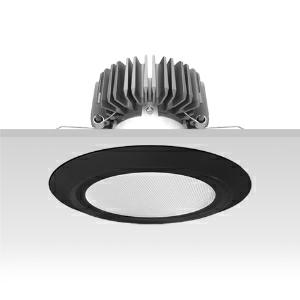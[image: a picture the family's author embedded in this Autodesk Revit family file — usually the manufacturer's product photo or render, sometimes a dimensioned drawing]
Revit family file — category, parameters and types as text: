
# Revit family: 3f_filippi_-_3f_reno_bianco_ampio_3f_filippi_-_30691_a01049_-_3f_reno_200_wh_4000-930_dali_wide___smp_bk_4fdb
name_source: partatom
category: Lighting Fixtures
units: mm (PartAtom-declared; Revit-internal decimal feet)

## family parameters
Cut with Voids When Loaded = No
Host = Face
Light Source = No
Part Type = Normal
Room Calculation Point = No
Round Connector Dimension = Use Diameter
Shared = No

## types (1)
- 3F Filippi - 3F Reno Bianco Ampio (1 x LED, 2801 lm, 43 W, 3000 K)
    Apparent Load = 43 VA
    Approval mark = CE
    CIE Flux Codes = 74 92 98 100 100
    Color Rendering = 90
    Color Temperature = 3000 K
    Control Gear = Electronic transformer
    Default Elevation = 1800 mm
    Description = ILLUMINOTECHNICAL
Luminous efficiency 100% (DLOR 100%, ULOR 0%).
Initial luminous flux of the luminaire 2801 lm.
Direct symmetric wide distribution.
Installation Interdistance Transv.D = 1.06 x hu - Long.D = 1.04 x hu.
Tabular UGR (CIE 117 - 4H-8H; S=0.25H; 70/50/20): RUG 23.1 - 23.
Beam angle: 70° - 69°.
Luminous efficacy 65 lm/W.
Lifetime (L90/B10): 30000 h. (tq+25°C)
Lifetime (L85/B10): 50000 h. (tq+25°C)
Lifetime (L70/B10): 80000 h. (tq+25°C)
Sudden decreased luminous flux after 50000 hours: 0% (C0).
Photobiological safety in compliance with IEC/TR 62778: RG1 low risk, (IEC 62471).
In compliance with IEC/EN 62722-2-1 - IEC/EN 62717 standards.

SOURCE
Compact LED module 4000/930.
Energy efficiency class (UE 2019/2020 - UE 2019/2015): F.
CIE 13.3 Colour rendering index: CRI >90 (R9 >50%).
IES TM-30 Fidelity Index: Rf = 92 Rg = 101.
CCT nominal colour temperature 3000 K.
Colour initial tolerance (MacAdam): SDCM 3.
Zhaga Book 3 compliant.

MECHANICAL
Passive heat dissipator in die-casting aluminium, oversized, for optimum thermal management of the LED module.
Parabolic element with graduated/concentric rings in white polycarbonate.
Transparent external lens with glossy and satin differentiated surfaces, with a cooling and anti-insect system in methacrylate (PMMA).
Fastening spring clips in stainless steel.
Dimensions: diameter 226 mm, height 146 mm. Weight 1.725 kg.
IP44 protection degree for exposed part, IP20 for recessed part.
Mechanical strength to impacts IK05 (0.7 joule).
Glow-wire test resistance 650°C.

ELECTRICAL
Wiring on a separate unit.
Halogen Free DALI-2 DATI (Parts 251, 252, 253), PUSH-DIM, electronic wiring 230V-50/60Hz, power factor 0.97 at full load, THD <25%, constant output current, SELV, class II, 1 driver, 1 DALI addresse.
Power of the luminaire 43 W.
ENEC - CE.
SAFE FLICKER: PstLM=<1 and SVM=<0.4 (IEC TR 61547-1 and IEC TR 63158), to ensure a more comfortable and safe light.
Luminaire compliant with EN 60598-2-22 for power supply from a centralised emergency system CPSS (Central Power Supply System), not incorporated in the luminaire - high risk areas excluded. The default power and flux are 100% in AC and 100% in DC.
Ambient temperature from 0°C to +25°C.
Temperature class T6 max 85°C.
Relative humidity UR: <85%.

INSTALLATION
Pull-up recessed fitting.
False ceiling carving: 200 mm.
All accessories dedicated to this product are available on the Catalog and on our website www.3F-Filippi.com.

ACCESSORIES
A01049 - Anti-glare microprismatic SMP diffuser in methacrylate (PMMA), locked and in line with the trim, in black polycarbonate.

APPLICATIONS
Suitable product for food production plants (HACCP), IFS (Food Version 6), BRC (GSFS Food Version 7).
Environments: architectural, commercial, exhibition areas, transit areas, corridors, shops, display windows, service areas.
In false ceilings with narrow voids.

LIGHT MANAGEMENT
Recommended minimum setting: 10%.
The luminaire, equipped with (DALI-2 DATI) driver, can be controlled manually with 3F Easy Dim technology or automatically/manually with wired or wireless DALI/D2D control systems.
The D2D driver guarantees interoperability with other devices with the same certification by making the following information available:
Device Data (Part 251), Energy Report (Part 252), Diagnosis & Maintenance (Part 253).
In electrical systems without a regulation system (manual or automatic) and DALI bus, a suitable jumper must be made on the DA-DA terminals of the appliance.

WARNING
Luminaire designed for disposal/recycling at end-of-life.
Replaceable (LED only) light source by a professional. Replaceable control gear by a professional.
    Height = 0 mm  [stored 0 ft]
    Lamp = 1 x LED
    Lamp Light Flux = 2801 lm
    Lamp Power = 43 W
    Lamp count = 1
    Length = 226 mm
    Lifetime = 50000 h
    Luminous efficacy = 65 lm/W
    Manufacturer = 3F Filippi
    ModVariant = No
    Model = 3F Filippi - 30691+A01049 - 3F Reno 200 WH 4000-930 DALI WIDE + SMP BK
    Mounting Place = Ceiling
    Mounting Type = Recessed
    Number of Poles = 1
    OnlyDefault = Yes
    Power Factor = 1
    Product Name = 3F Filippi - 3F Reno Bianco Ampio
    Product group = recessed luminaire
    ProductGroupID = 4
    Protection Class = Protection class II
    Protection Degree = IP 20
    RLX_Detail_Level = 1
    RLX_Emergency_Light_Flux = 0 lm
    RLX_Emergency_Type = 0
    RLX_Emergency_Type_DB = No
    RlxData = <blob elided: 100477 chars, md5=96b07a52>
    Socket = socket
    Standby Power = 0 W
    System Light Flux = 2801 lm
    System Power = 43 W
    Type Comments = Product without accessories
    Type Image = 3ffilippi_3f_reno_200_bk_vs_smp.jpg
    URL = http://relux.com
    VarID = ---
    Voltage = 0 V
    Weight = 0.00 kg
    Width = 0 mm  [stored 0 ft]

note: [stored X ft] marks values corroborated as IEEE doubles in the binary element streams (Revit-internal decimal feet)

## geometry (parser evidence)
native form markers: Blend x4, Sweep x10
no freeform markers — native parametric forms only
